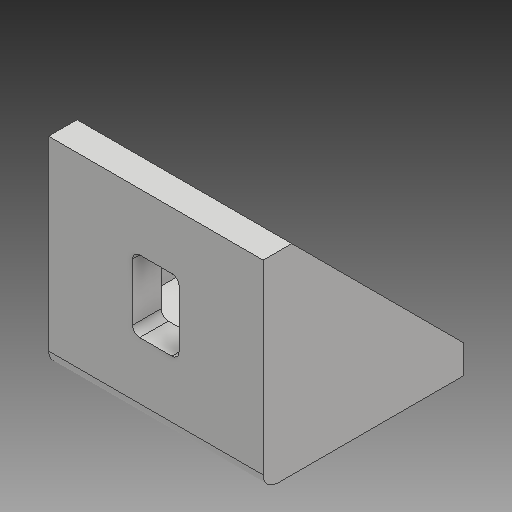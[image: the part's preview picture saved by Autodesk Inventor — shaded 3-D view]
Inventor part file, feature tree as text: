
AUTODESK INVENTOR PART (.ipt)
format: ipt  version: 2018 (Build 220112000, 112)  size: 165,888 bytes
history: native  units: mm
features: extrude x5, sketch x5, projected_geometry x4
ambient origin geometry x8: Origin, YZ Plane, XZ Plane, XY Plane, X Axis, Y Axis, Z Axis, Center Point
bodies: Volumenkörper1 (feature_tree)
feature tree (14):
  extrude  "Extrusion1"  Depth=2.8mm
  extrude  "Extrusion2"  Depth=0.4mm
  extrude  "Extrusion3"  Depth=0.4mm
  extrude  "Extrusion4"  Depth=0.2mm TaperAngle=0.0deg
  extrude  "Extrusion5"  Depth=0.65mm
  sketch  "Skizze2"  dims[d0=2.8mm d1=2.8mm]
  sketch  "Skizze3"  dims[d2=0.4mm d3=0.4mm]
  projected_geometry  "Projizierte Kontur1"
  sketch  "Skizze4"  dims[d4=0.2mm d5=0.4mm]
  projected_geometry  "Projizierte Kontur2"
  sketch  "Skizze5"  dims[d6=2.6mm d7=0.0mm d8=0.2mm d9=0.0mm]
  projected_geometry  "Projizierte Kontur3"
  sketch  "Skizze6"  dims[d10=0.2mm d11=0.0mm d12=0.65mm d13=1.0mm d14=0.1mm d15=0.4mm d16=0.0mm d17=1.0mm d18=0.65mm d19=0.1mm d20=0.4mm d21=0.0mm]
  projected_geometry  "Projizierte Kontur4"
